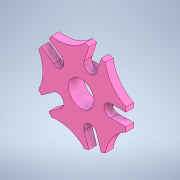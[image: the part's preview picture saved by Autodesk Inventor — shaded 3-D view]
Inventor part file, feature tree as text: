
AUTODESK INVENTOR PART (.ipt)
format: ipt  version: 2022 (Build 260153000, 153)  size: 182,784 bytes
history: native  units: mm
features: extrude x5, sketch x5, pattern_circular x2, other x1, fillet x1
ambient origin geometry x8: Origin, YZ Plane, XZ Plane, XY Plane, X Axis, Y Axis, Z Axis, Center Point
bodies: Body1 (feature_tree)
feature tree (14):
  other  "Sólido1"
  extrude  "Extrusão1"  Depth=6.0mm TaperAngle=0.0deg
  extrude  "Extrusão2"  Depth=30.0mm
  fillet  "Arredondamento1"  Radius=30.0mm
  pattern_circular  "Padrão circular1"  [2 undecoded]
  extrude  "Extrusão3"  Depth=6.0mm TaperAngle=360.0deg
  extrude  "Extrusão4"  Depth=6.0mm
  pattern_circular  "Padrão circular2"  [2 undecoded]
  extrude  "Extrusão5"  Depth=6.0mm
  sketch  "Esboço1"  dims[d9=100.0mm d10=6.0mm d11=0.0mm]
  sketch  "Esboço2"  dims[d12=35.0mm d13=100.0mm d14=30.0mm]
  sketch  "Esboço3"  dims[d15=10.0mm]
  sketch  "Esboço4"  dims[d16=18.0mm]
  sketch  "Esboço5"  dims[d17=6.0mm d18=0.0mm d19=5.0mm d20=50.0mm d21=360.0deg d23=20.0mm d24=0.0mm d25=0.0mm d26=60.0mm d27=60.0mm d28=0.0mm d29=0.0mm d30=50.0mm d31=360.0deg d33=30.0mm d34=6.0mm d35=0.0mm d22=0.0mm]
note: 4 required parameter values undecoded (feature->parameter linkage not recoverable at this tier; creation-order binding heuristic only, values carry confidence <= 0.55)
